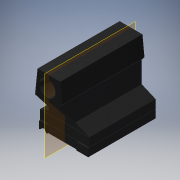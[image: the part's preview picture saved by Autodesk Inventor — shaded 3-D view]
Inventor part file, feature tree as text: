
AUTODESK INVENTOR PART (.ipt)
format: ipt  version: 2018 (Build 220112000, 112)  size: 502,272 bytes
history: native  units: mm
features: extrude x26, sketch x26, fillet x6, plane x2
ambient origin geometry x8: Origin, YZ Plane, XZ Plane, XY Plane, X Axis, Y Axis, Z Axis, Center Point
bodies: Solid1 (feature_tree)
feature tree (60):
  extrude  "Extrusion1"  Depth=151.0mm
  extrude  "Extrusion2"  Depth=203.0mm
  extrude  "Extrusion3"  TaperAngle=135.0deg  [1 undecoded]
  extrude  "Extrusion4"  Depth=10.0mm
  extrude  "Extrusion5"  Depth=28.0mm
  extrude  "Extrusion6"  Depth=2.0mm TaperAngle=0.0deg
  fillet  "Fillet1"  Radius=37.0mm
  extrude  "Extrusion7"  Depth=1.0mm TaperAngle=0.0deg
  fillet  "Fillet3"  Radius=5.0mm
  extrude  "Extrusion8"  Depth=5.0mm
  extrude  "Extrusion9"  Depth=1.0mm
  extrude  "Extrusion10"  Depth=1.0mm
  extrude  "Extrusion11"  Depth=1.0mm TaperAngle=0.0deg
  plane  "Work Plane1"
  extrude  "Extrusion12"  Depth=49.0mm TaperAngle=0.0deg
  extrude  "Extrusion13"  Depth=35.0mm
  extrude  "Extrusion14"  Depth=16.755161mm
  extrude  "Extrusion15"  Depth=295.5mm TaperAngle=0.0deg
  fillet  "Fillet4"  Radius=295.5mm
  extrude  "Extrusion16"  Depth=295.5mm TaperAngle=0.0deg
  extrude  "Extrusion17"  Depth=2.0mm
  plane  "Work Plane2"
  extrude  "Extrusion18"  Depth=50.0mm
  extrude  "Extrusion19"  Depth=5.0mm TaperAngle=0.0deg
  extrude  "Extrusion20"  Depth=1.0mm TaperAngle=0.0deg
  extrude  "Extrusion21"  Depth=207.0mm TaperAngle=0.0deg
  extrude  "Extrusion22"  Depth=204.0mm
  extrude  "Extrusion23"  Depth=6.981317mm
  extrude  "Extrusion24"  Depth=204.0mm TaperAngle=0.0deg
  fillet  "Fillet5"  Radius=25.3mm
  fillet  "Fillet6"  Radius=3.0mm
  extrude  "Extrusion25"  Depth=3.0mm
  fillet  "Fillet7"  Radius=36.2mm
  extrude  "Extrusion26"  Depth=3.0mm
  sketch  "Sketch1"  dims[d19=26.0mm d20=151.0mm]
  sketch  "Sketch2"  dims[d21=203.0mm d22=0.0mm d23=28.0mm]
  sketch  "Sketch3"  dims[d29=4.0mm d30=135.0deg]
  sketch  "Sketch4"  dims[d31=45.0deg d32=10.0mm]
  sketch  "Sketch5"  dims[d33=215.0mm d34=0.0mm d35=28.0mm]
  sketch  "Sketch6"  dims[d36=6.0mm d37=0.0mm d38=2.0mm d39=0.0mm d40=37.0mm]
  sketch  "Sketch8"  dims[d41=6.0mm d42=0.0mm d43=1.0mm d44=0.0mm d45=5.0mm]
  sketch  "Sketch9"  dims[d47=1.0mm d48=0.0mm d49=5.0mm]
  sketch  "Sketch10"  dims[d50=1.0mm d51=1.0mm]
  sketch  "Sketch11"  dims[d52=1.0mm d53=1.0mm]
  sketch  "Sketch12"  dims[d54=1.0mm d55=0.0mm d56=26.0mm d57=0.0mm]
  sketch  "Sketch13"  dims[d58=49.0mm d59=152.0mm d60=0.0mm]
  sketch  "Sketch14"  dims[d61=35.0mm d62=35.0mm]
  sketch  "Sketch15"  dims[d63=16.755161mm d64=16.755161mm]
  sketch  "Sketch16"  dims[d65=58.0mm d66=295.5mm d67=0.0mm d68=295.5mm d69=0.0mm]
  sketch  "Sketch18"  dims[d70=295.5mm d71=0.0mm d72=295.5mm d73=0.0mm]
  sketch  "Sketch19"  dims[d74=1.0mm d75=0.0mm d76=2.0mm]
  sketch  "Sketch20"  dims[d85=1.0mm d86=0.0mm d87=50.0mm]
  sketch  "Sketch21"  dims[d88=300.0mm d89=0.0mm d90=5.0mm d91=0.0mm]
  sketch  "Sketch23"  dims[d92=1.0mm d93=0.0mm d94=1.0mm d95=0.0mm]
  sketch  "Sketch24"  dims[d96=2.0mm d97=207.0mm d98=0.0mm]
  sketch  "Sketch25"  dims[d99=204.0mm d100=0.0mm d101=148.124mm]
  sketch  "Sketch26"  dims[d102=10.2mm d103=6.981317mm]
  sketch  "Sketch27"  dims[d104=3.8mm d106=204.0mm d107=0.0mm d108=25.3mm d109=3.0mm d110=0.0mm]
  sketch  "Sketch28"  dims[d111=3.0mm d112=3.0mm d113=36.2mm]
  sketch  "Sketch29"  dims[d114=3.0mm d115=0.0mm d116=3.0mm d117=2.0mm d118=24.43461mm d121=4.0mm d122=8.0mm d123=22.68928mm d124=10.0mm d125=0.0mm d126=30.0mm]
note: 1 required parameter value undecoded (feature->parameter linkage not recoverable at this tier; creation-order binding heuristic only, values carry confidence <= 0.55)
